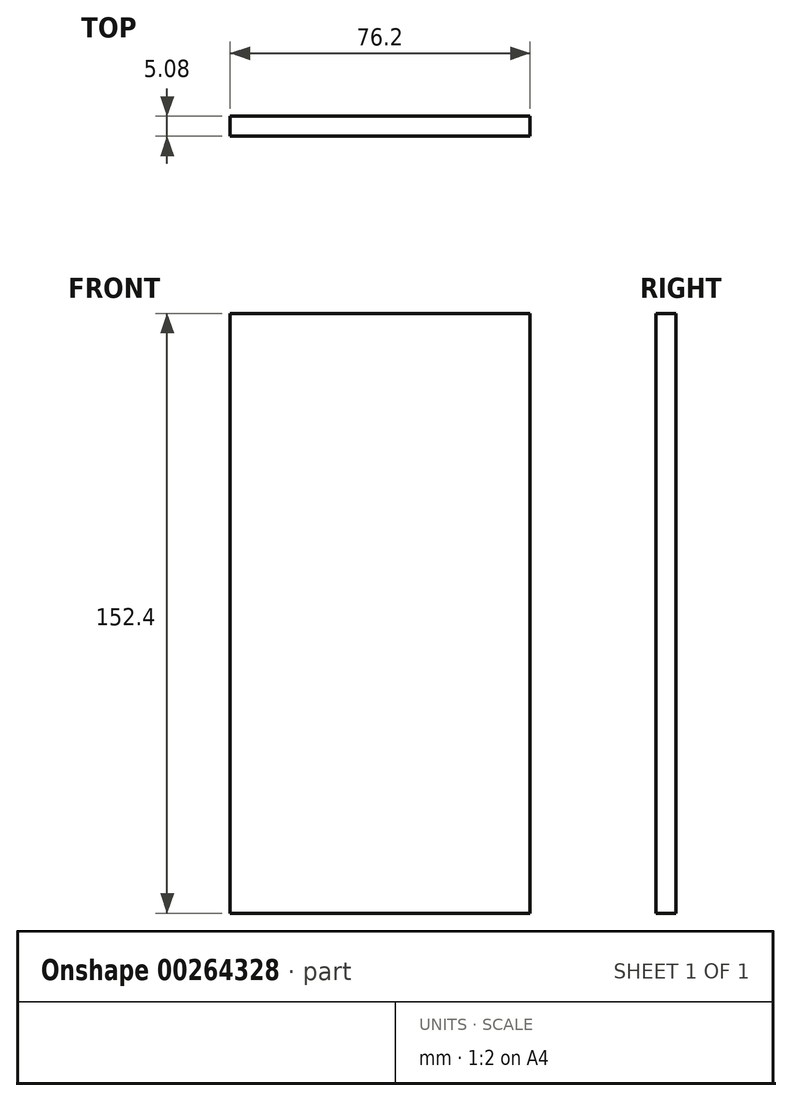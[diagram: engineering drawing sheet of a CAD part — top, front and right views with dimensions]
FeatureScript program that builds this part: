
annotation { "Feature Type Name" : "Feature", "Feature Type Description" : "" }
export const myFeature = defineFeature(function(context is Context, id is Id, definition is map)
    precondition{}
    {
        {
            var Q0;
            Q0=qCreatedBy(makeId("Front.planeOp"),FACE);
            var sketch = newSketch(context, id + "F0", { "sketchPlane" : qUnion([Q0])});
            skLineSegment(sketch, "E0.bottom", {"start": v(38.1, 74.52) * mm, "end": v(-38.1, 74.52) * mm});
            skLineSegment(sketch, "E0.top", {"start": v(38.1, -77.88) * mm, "end": v(-38.1, -77.88) * mm});
            skLineSegment(sketch, "E0.left", {"start": v(38.1, 74.52) * mm, "end": v(38.1, -77.88) * mm});
            skLineSegment(sketch, "E0.right", {"start": v(-38.1, 74.52) * mm, "end": v(-38.1, -77.88) * mm});
            skPoint(sketch, "E0.middle", {"position": v(0, -1.68) * mm});
            skSolve(sketch);
        }
        {
            var Q0;
            Q0=makeQuery(id+"F0.imprint","IMPRINT",FACE,{"disambiguationData":[TD([[makeQuery(id+"F0.imprint","IMPRINT",EDGE,{"derivedFrom":sQuery(id+"F0.wireOp",EDGE,"E0.bottom")}),1.0]])]});
            extrude(context, id + "F1", {"entities" : qUnion([Q0]), "oppositeDirection" : true, "depth" : 5.08 * mm});
        }
    });
